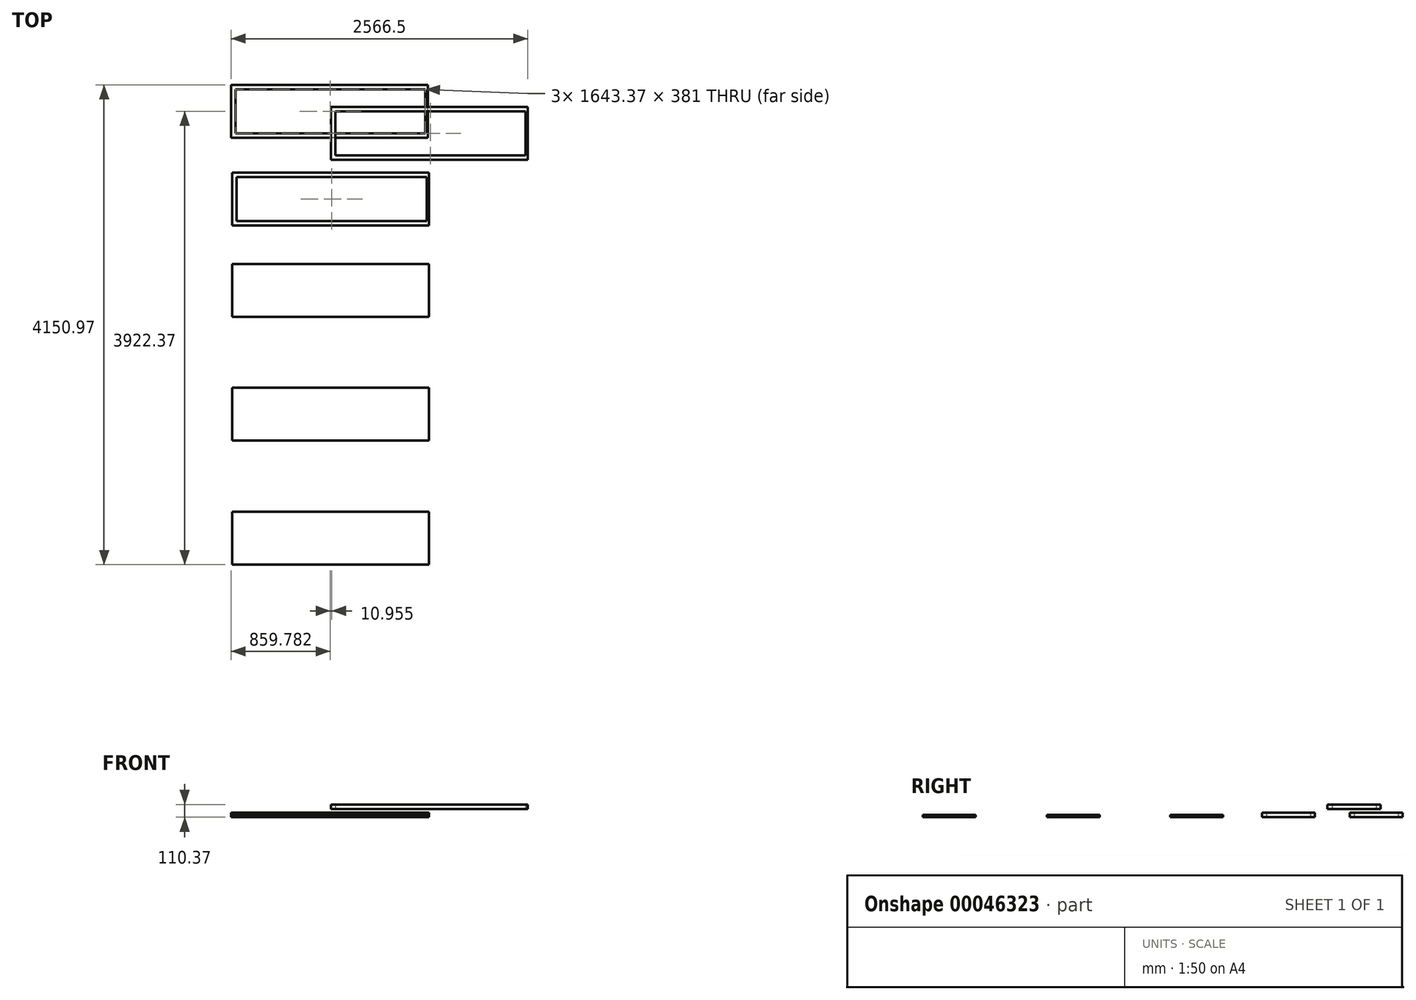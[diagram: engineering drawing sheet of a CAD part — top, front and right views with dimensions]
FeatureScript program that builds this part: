
annotation { "Feature Type Name" : "Feature", "Feature Type Description" : "" }
export const myFeature = defineFeature(function(context is Context, id is Id, definition is map)
    precondition{}
    {
        {
            var Q0;
            Q0=qCreatedBy(makeId("Top.planeOp"),FACE);
            var sketch = newSketch(context, id + "F0", { "sketchPlane" : qUnion([Q0])});
            skLineSegment(sketch, "E0.bottom", {"start": v(0, 457.2) * mm, "end": v(-1701.8, 457.2) * mm});
            skLineSegment(sketch, "E0.top", {"start": v(0, 0) * mm, "end": v(-1701.8, 0) * mm});
            skLineSegment(sketch, "E0.left", {"start": v(0, 457.2) * mm, "end": v(0, 0) * mm});
            skLineSegment(sketch, "E0.right", {"start": v(-1701.8, 457.2) * mm, "end": v(-1701.8, 0) * mm});
            skSolve(sketch);
        }
        {
            var Q0;
            Q0=makeQuery(id+"F0.imprint","IMPRINT",FACE,{"disambiguationData":[TD([[makeQuery(id+"F0.imprint","IMPRINT",EDGE,{"derivedFrom":sQuery(id+"F0.wireOp",EDGE,"E0.bottom")}),1.0]])]});
            extrude(context, id + "F1", {"entities" : qUnion([Q0]), "depth" : 19.05 * mm});
        }
        {
            var Q0;
            Q0=qCreatedBy(makeId("Top.planeOp"),FACE);
            var sketch = newSketch(context, id + "F2", { "sketchPlane" : qUnion([Q0])});
            skLineSegment(sketch, "E1.bottom", {"start": v(-1701.8, -609.79) * mm, "end": v(0, -609.79) * mm});
            skLineSegment(sketch, "E1.top", {"start": v(-1701.8, -1066.99) * mm, "end": v(0, -1066.99) * mm});
            skLineSegment(sketch, "E1.left", {"start": v(-1701.8, -609.79) * mm, "end": v(-1701.8, -1066.99) * mm});
            skLineSegment(sketch, "E1.right", {"start": v(0, -609.79) * mm, "end": v(0, -1066.99) * mm});
            skSolve(sketch);
        }
        {
            var Q0;
            Q0=makeQuery(id+"F2.imprint","IMPRINT",FACE,{"disambiguationData":[TD([[makeQuery(id+"F2.imprint","IMPRINT",EDGE,{"derivedFrom":sQuery(id+"F2.wireOp",EDGE,"E1.bottom")}),-1.0]])]});
            extrude(context, id + "F3", {"entities" : qUnion([Q0]), "depth" : 19.05 * mm});
        }
        {
            var Q0;
            Q0=makeQuery(id+"F3.opExtrude","SWEPT_BODY",BODY,{"disambiguationData":[OSD([sQuery(id+"F2.wireOp",EDGE,"E1.bottom"),sQuery(id+"F2.wireOp",EDGE,"E1.top"),sQuery(id+"F2.wireOp",EDGE,"E1.left"),sQuery(id+"F2.wireOp",EDGE,"E1.right")])]});
            transform(context, id + "F4", {"entities" : qUnion([Q0]), "transformType" : TransformType.TRANSLATION_3D, "dx" : 0 * mm, "dy" : -1074.87 * mm, "dz" : 0 * mm, "makeCopy" : true});
        }
        {
            var Q0;
            Q0=qCreatedBy(makeId("Top.planeOp"),FACE);
            var sketch = newSketch(context, id + "F5", { "sketchPlane" : qUnion([Q0])});
            skLineSegment(sketch, "E2.bottom", {"start": v(0, 792.76) * mm, "end": v(-1701.8, 792.76) * mm});
            skLineSegment(sketch, "E2.top", {"start": v(0, 1249.96) * mm, "end": v(-1701.8, 1249.96) * mm});
            skLineSegment(sketch, "E2.left", {"start": v(0, 830.86) * mm, "end": v(0, 1211.86) * mm});
            skLineSegment(sketch, "E2.right", {"start": v(-1701.8, 792.76) * mm, "end": v(-1701.8, 1249.96) * mm});
            skLineSegment(sketch, "E3", {"start": v(0, 1211.86) * mm, "end": v(-1663.7, 1211.86) * mm});
            skLineSegment(sketch, "E4", {"start": v(0, 830.86) * mm, "end": v(-1663.7, 830.86) * mm});
            skLineSegment(sketch, "E5", {"start": v(0, 1211.86) * mm, "end": v(0, 1249.96) * mm});
            skLineSegment(sketch, "E6", {"start": v(0, 792.76) * mm, "end": v(0, 830.86) * mm});
            skLineSegment(sketch, "E7", {"start": v(-20.33, 792.76) * mm, "end": v(-20.33, 1249.96) * mm});
            skLineSegment(sketch, "E8", {"start": v(-1663.7, 830.86) * mm, "end": v(-1663.7, 1211.86) * mm});
            skPoint(sketch, "E9.orphan", {"position": v(-1701.8, 830.86) * mm});
            skPoint(sketch, "E10.orphan", {"position": v(-1701.8, 1211.86) * mm});
            skLineSegment(sketch, "E11", {"start": v(-1663.7, 830.86) * mm, "end": v(-1701.8, 830.86) * mm});
            skLineSegment(sketch, "E12", {"start": v(-1663.7, 1211.86) * mm, "end": v(-1701.8, 1211.86) * mm});
            skSolve(sketch);
        }
        {
            var Q0;
            {var subQ0=sQuery(id+"F5.wireOp",EDGE,"E11");Q0=makeQuery(id+"F5.imprint","IMPRINT",FACE,{"disambiguationData":[TD([[makeQuery(id+"F5.imprint","IMPRINT",EDGE,{"derivedFrom":subQ0}),1.0]])]});}
            var Q1;
            Q1=makeQuery(id+"F5.imprint","IMPRINT",FACE,{"disambiguationData":[TD([[makeQuery(id+"F5.imprint","IMPRINT",EDGE,{"derivedFrom":sQuery(id+"F5.wireOp",EDGE,"E8")}),1.0]])]});
            var Q2;
            {var subQ0=sQuery(id+"F5.wireOp",EDGE,"E12");Q2=makeQuery(id+"F5.imprint","IMPRINT",FACE,{"disambiguationData":[TD([[makeQuery(id+"F5.imprint","IMPRINT",EDGE,{"derivedFrom":subQ0}),-1.0]])]});}
            var Q3;
            {var subQ5=sQuery(id+"F5.wireOp",EDGE,"E6");Q3=makeQuery(id+"F5.imprint","IMPRINT",FACE,{"disambiguationData":[TD([[makeQuery(id+"F5.imprint","IMPRINT",EDGE,{"derivedFrom":subQ5}),1.0]])]});}
            var Q4;
            {var subQ5=sQuery(id+"F5.wireOp",EDGE,"E2.left");Q4=makeQuery(id+"F5.imprint","IMPRINT",FACE,{"disambiguationData":[TD([[makeQuery(id+"F5.imprint","IMPRINT",EDGE,{"derivedFrom":subQ5}),1.0]])]});}
            var Q5;
            {var subQ5=sQuery(id+"F5.wireOp",EDGE,"E5");Q5=makeQuery(id+"F5.imprint","IMPRINT",FACE,{"disambiguationData":[TD([[makeQuery(id+"F5.imprint","IMPRINT",EDGE,{"derivedFrom":subQ5}),1.0]])]});}
            extrude(context, id + "F6", {"entities" : qUnion([Q0, Q1, Q2, Q3, Q4, Q5]), "depth" : 38.1 * mm});
        }
        {
            var Q0;
            Q0=makeQuery(id+"F6.opExtrude","SWEPT_BODY",BODY,{"disambiguationData":[OSD([sQuery(id+"F5.wireOp",EDGE,"E2.bottom"),sQuery(id+"F5.wireOp",EDGE,"E2.top"),sQuery(id+"F5.wireOp",EDGE,"E2.left"),sQuery(id+"F5.wireOp",EDGE,"E2.right"),sQuery(id+"F5.wireOp",EDGE,"E3"),sQuery(id+"F5.wireOp",EDGE,"E4"),sQuery(id+"F5.wireOp",EDGE,"E5"),sQuery(id+"F5.wireOp",EDGE,"E6"),sQuery(id+"F5.wireOp",EDGE,"E7"),sQuery(id+"F5.wireOp",EDGE,"E8")])]});
            transform(context, id + "F7", {"entities" : qUnion([Q0]), "transformType" : TransformType.TRANSLATION_3D, "dx" : 853.75 * mm, "dy" : 567.24 * mm, "dz" : 72.27 * mm, "makeCopy" : true});
        }
        {
            var Q0;
            Q0=makeQuery(id+"F6.opExtrude","SWEPT_BODY",BODY,{"disambiguationData":[OSD([sQuery(id+"F5.wireOp",EDGE,"E2.bottom"),sQuery(id+"F5.wireOp",EDGE,"E2.top"),sQuery(id+"F5.wireOp",EDGE,"E2.left"),sQuery(id+"F5.wireOp",EDGE,"E2.right"),sQuery(id+"F5.wireOp",EDGE,"E3"),sQuery(id+"F5.wireOp",EDGE,"E4"),sQuery(id+"F5.wireOp",EDGE,"E5"),sQuery(id+"F5.wireOp",EDGE,"E6"),sQuery(id+"F5.wireOp",EDGE,"E7"),sQuery(id+"F5.wireOp",EDGE,"E8")])]});
            transform(context, id + "F8", {"entities" : qUnion([Q0]), "transformType" : TransformType.TRANSLATION_3D, "dx" : -10.95 * mm, "dy" : 759.16 * mm, "dz" : 0 * mm, "makeCopy" : true});
        }
    });
